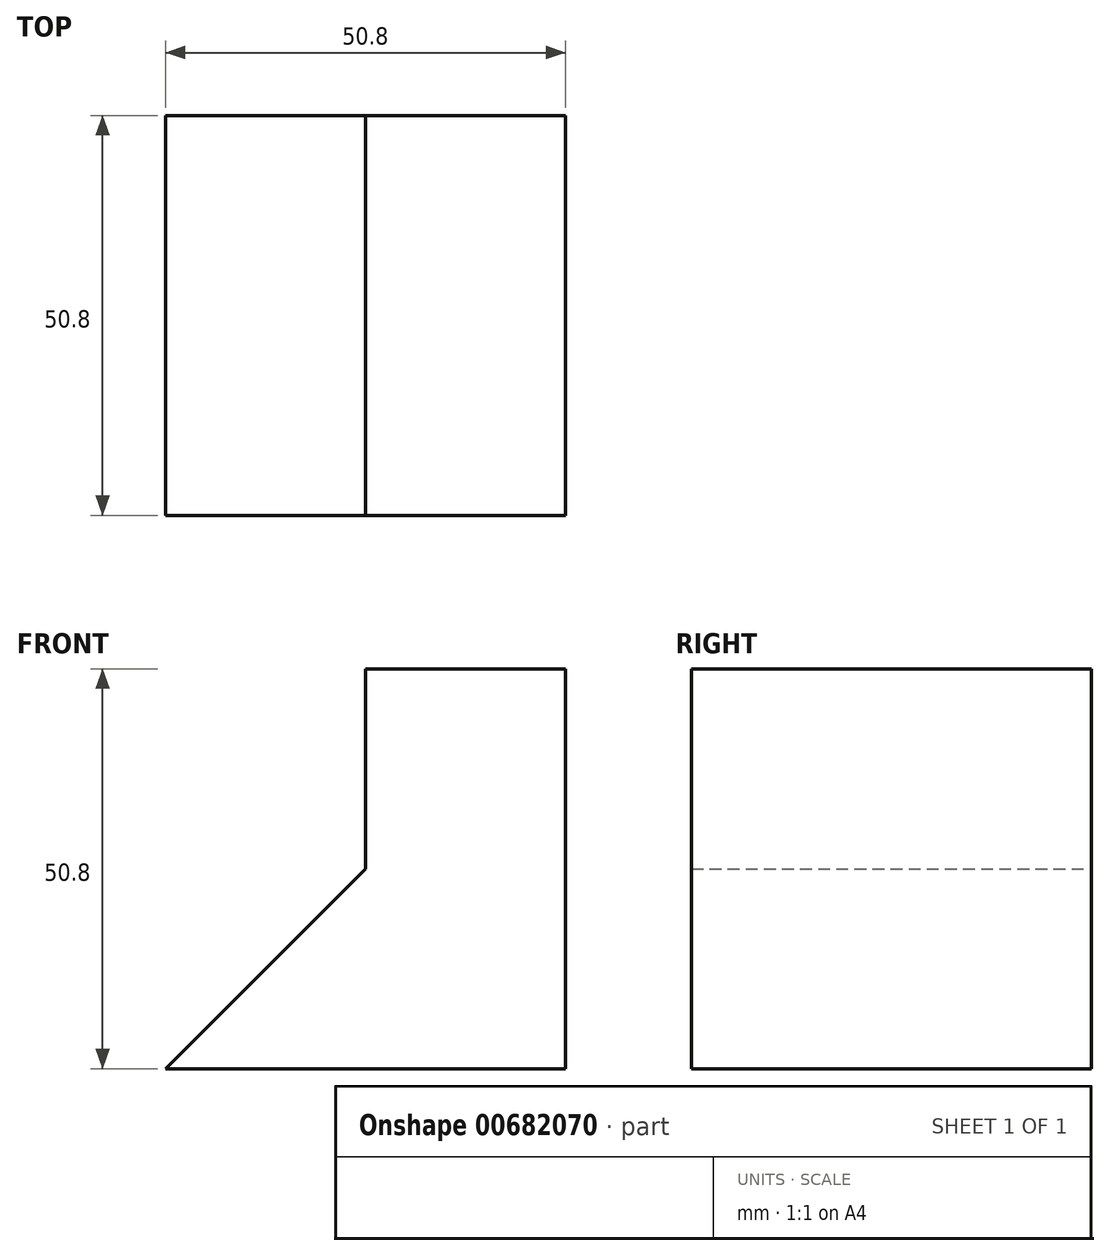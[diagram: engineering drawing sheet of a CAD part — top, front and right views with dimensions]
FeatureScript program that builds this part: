
annotation { "Feature Type Name" : "Feature", "Feature Type Description" : "" }
export const myFeature = defineFeature(function(context is Context, id is Id, definition is map)
    precondition{}
    {
        {
            var Q0;
            Q0=qCreatedBy(makeId("Front.planeOp"),FACE);
            var sketch = newSketch(context, id + "F0", { "sketchPlane" : qUnion([Q0])});
            skLineSegment(sketch, "E0", {"start": v(0, 0) * mm, "end": v(-50.8, 0) * mm});
            skLineSegment(sketch, "E1", {"start": v(0, 0) * mm, "end": v(0, 50.8) * mm});
            skLineSegment(sketch, "E2", {"start": v(0, 50.8) * mm, "end": v(-25.4, 50.8) * mm});
            skLineSegment(sketch, "E3", {"start": v(-25.4, 50.8) * mm, "end": v(-25.4, 25.4) * mm});
            skLineSegment(sketch, "E4", {"start": v(-25.4, 25.4) * mm, "end": v(-50.8, 0) * mm});
            skSolve(sketch);
        }
        {
            var Q0;
            Q0 = qSketchRegion(id + "F0", true);
            extrude(context, id + "F1", {"entities" : qUnion([Q0]), "depth" : 50.8 * mm, "offsetDistance" : 25.4 * mm});
        }
    });
